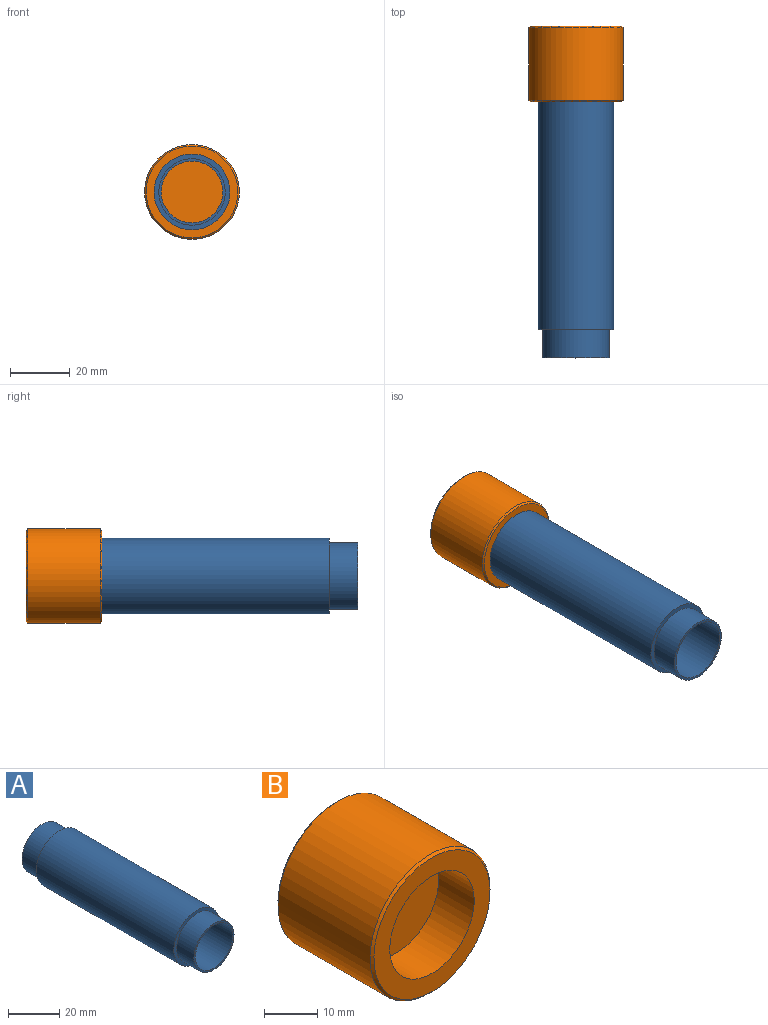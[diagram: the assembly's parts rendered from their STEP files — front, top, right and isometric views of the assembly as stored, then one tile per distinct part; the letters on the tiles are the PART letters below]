
ASSEMBLY  parts=2 mates=1
PART A: 8 faces, bbox 25.4x95.3x25.4 mm
  f0: cylinder r=11.11mm len=22.23mm, axis (0,1,0), area 665.1mm2, adj f4,f7
  f1: cylinder r=10.32mm len=95.25mm, axis (0,1,0), area 6175.5mm2, adj f3,f4
  f2: cylinder r=11.11mm len=22.23mm, axis (0,1,0), area 665.1mm2, adj f3,f6
  f3: plane 22.23x22.23mm, normal (0,-1,0), area 53.4mm2, adj f1,f2
  f4: plane 22.23x22.23mm, normal (0,1,0), area 53.4mm2, adj f0,f1
  f5: cylinder r=12.7mm len=76.2mm, axis (0,1,0), area 6080.5mm2, adj f6,f7
  f6: plane 25.4x25.4mm, normal (0,-1,0), area 118.8mm2, adj f2,f5
  f7: plane 25.4x25.4mm, normal (0,1,0), area 118.8mm2, adj f0,f5
PART B: 7 faces, bbox 31.8x25.4x31.8 mm
  f0: plane 22.35x22.35mm, normal (0,-1,0), area 392.4mm2, adj f1
  f1: cylinder r=11.18mm len=22.35mm, axis (0,1,0), area 659.9mm2, adj f0,f3
  f2: cylinder r=15.88mm len=31.75mm, axis (0,1,0), area 2432.2mm2, adj f5,f6
  f3: plane 30.73x30.73mm, normal (0,-1,0), area 349.5mm2, adj f1,f5
  f4: plane 30.73x30.73mm, normal (0,1,0), area 741.9mm2, adj f6
  f5: cone r=15.37mm half-angle=45deg, axis (0,1,0), area 70.5mm2, adj f2,f3
  f6: cone r=15.88mm half-angle=45deg, axis (0,-1,0), area 70.5mm2, adj f2,f4
PLACE A rot(axis=(0,1,0),0.1deg) t=(-1,22.32,1.06)mm
PLACE B t=(-1,85.86,1.06)mm
MATE cylindrical A.f0 <-> B.f2  axis (0,1,0) through (-1,69.95,1.06)mm
